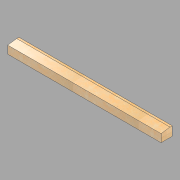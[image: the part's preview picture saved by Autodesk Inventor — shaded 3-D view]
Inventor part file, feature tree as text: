
AUTODESK INVENTOR PART (.ipt)
format: ipt  version: 2022.1 (Build 261234020, 234B)  size: 98,304 bytes
history: native  units: in
note: dims shown in document units (in); Inventor stores cm internally (conversion verified against a paired STEP export)
features: extrude x1, sketch x1
ambient origin geometry x8: Origin, YZ Plane, XZ Plane, XY Plane, X Axis, Y Axis, Z Axis, Center Point
bodies: Solid1 (feature_tree)
feature tree (2):
  extrude  "Extrusion1"  Depth=5.0in
  sketch  "Sketch1"  dims[d0=4.0in d1=5.0in d2=3.5in d3=1.0in d4=68.125in d5=0.0in]
